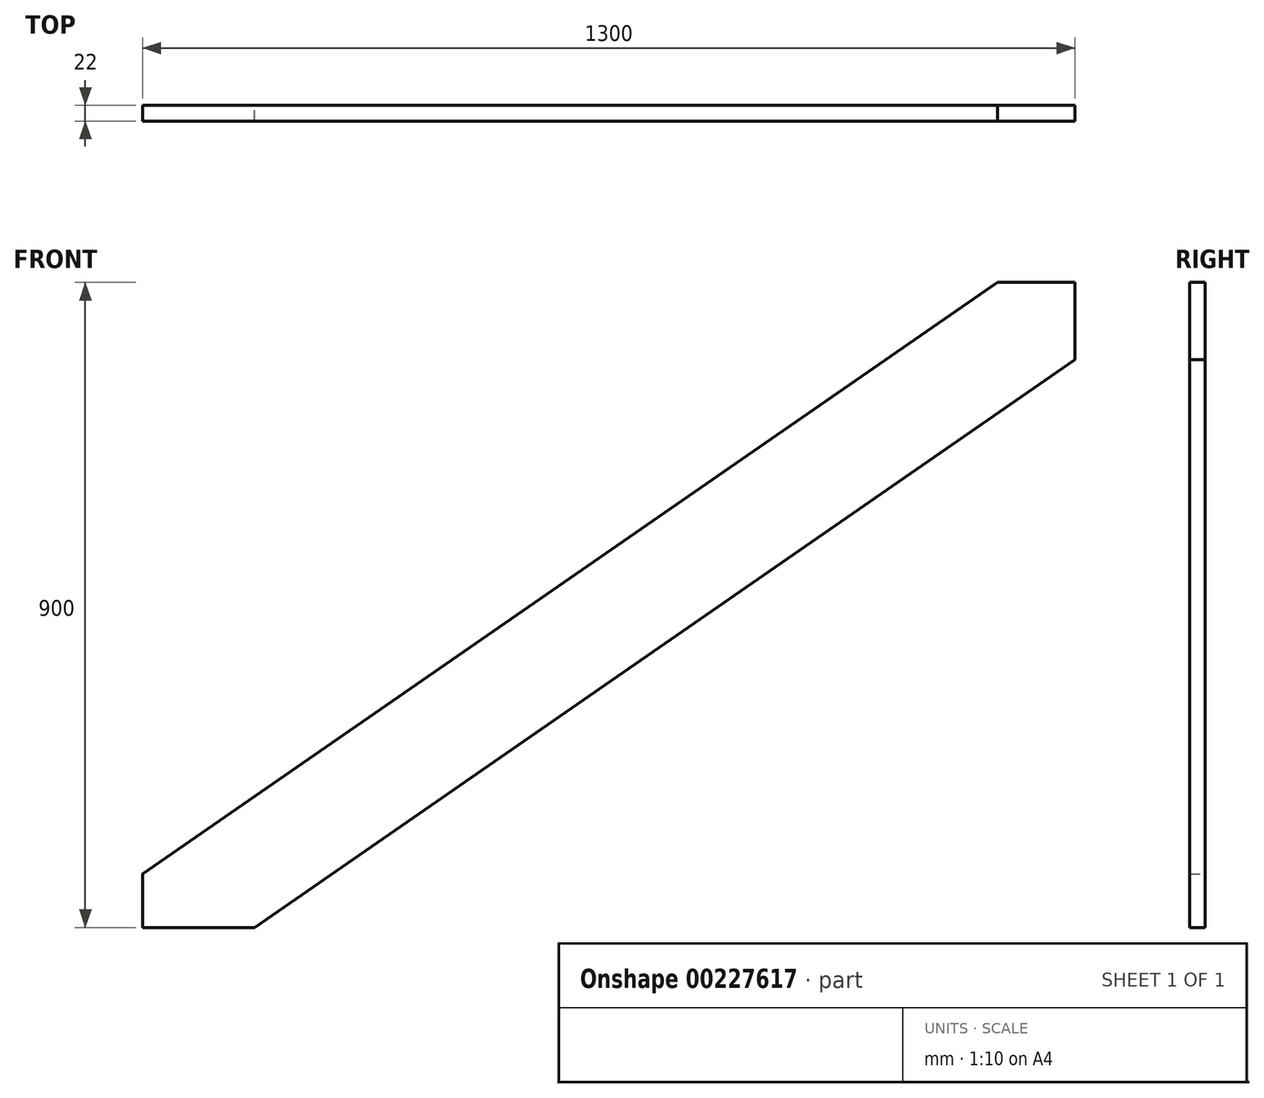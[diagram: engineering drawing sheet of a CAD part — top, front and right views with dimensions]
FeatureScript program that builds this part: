
annotation { "Feature Type Name" : "Feature", "Feature Type Description" : "" }
export const myFeature = defineFeature(function(context is Context, id is Id, definition is map)
    precondition{}
    {
        {
            var Q0;
            Q0=qCreatedBy(makeId("Front.planeOp"),FACE);
            var sketch = newSketch(context, id + "F0", { "sketchPlane" : qUnion([Q0])});
            skLineSegment(sketch, "E0.bottom", {"start": v(650, 450) * mm, "end": v(-650, 450) * mm, "construction": true});
            skLineSegment(sketch, "E0.top", {"start": v(650, -450) * mm, "end": v(-650, -450) * mm, "construction": true});
            skLineSegment(sketch, "E0.left", {"start": v(650, 450) * mm, "end": v(650, -450) * mm, "construction": true});
            skLineSegment(sketch, "E0.right", {"start": v(-650, 450) * mm, "end": v(-650, -450) * mm, "construction": true});
            skPoint(sketch, "E0.middle", {"position": v(0, 0) * mm});
            skLineSegment(sketch, "E1", {"start": v(-650, -450) * mm, "end": v(650, 450) * mm, "construction": true});
            skLineSegment(sketch, "E2", {"start": v(542.2, 450) * mm, "end": v(-650, -375.37) * mm});
            skLineSegment(sketch, "E3", {"start": v(-494.28, -450) * mm, "end": v(650, 342.2) * mm});
            skLineSegment(sketch, "E4", {"start": v(650, 342.2) * mm, "end": v(650, 450) * mm});
            skLineSegment(sketch, "E5", {"start": v(542.2, 450) * mm, "end": v(650, 450) * mm});
            skLineSegment(sketch, "E6", {"start": v(-494.28, -450) * mm, "end": v(-650, -450) * mm});
            skLineSegment(sketch, "E7", {"start": v(-650, -450) * mm, "end": v(-650, -375.37) * mm});
            skSolve(sketch);
        }
        {
            var Q0;
            Q0 = qSketchRegion(id + "F0", true);
            extrude(context, id + "F1", {"entities" : qUnion([Q0]), "depth" : 22 * mm});
        }
    });
